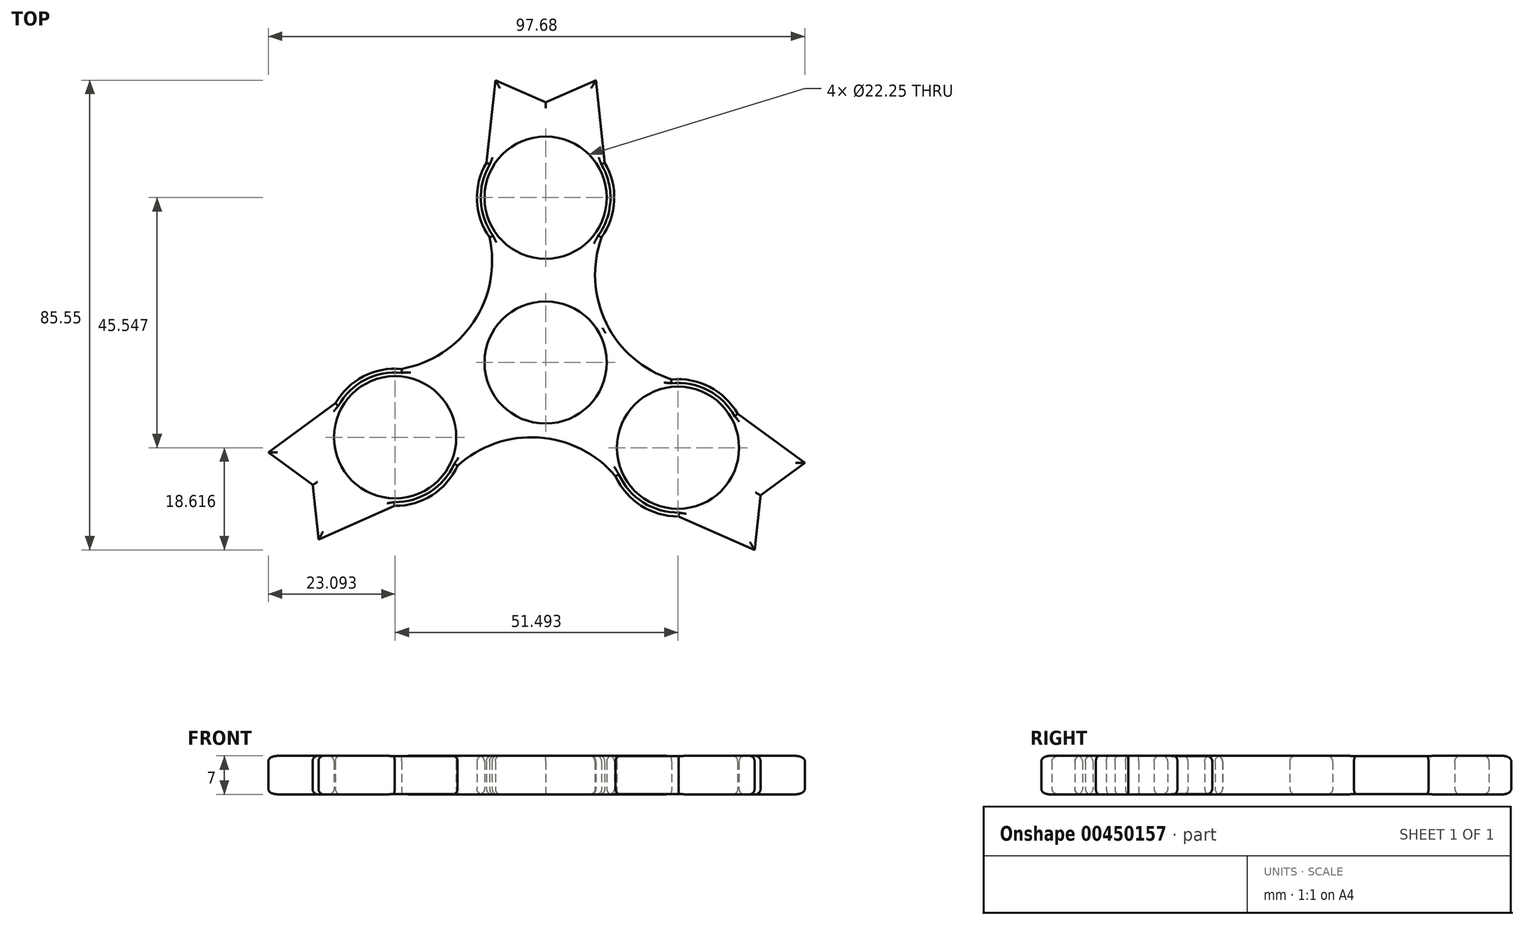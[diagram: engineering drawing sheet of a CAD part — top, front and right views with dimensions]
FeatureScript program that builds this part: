
annotation { "Feature Type Name" : "Feature", "Feature Type Description" : "" }
export const myFeature = defineFeature(function(context is Context, id is Id, definition is map)
    precondition{}
    {
        {
            var Q0;
            Q0=qCreatedBy(makeId("Top.planeOp"),FACE);
            var sketch = newSketch(context, id + "F0", { "sketchPlane" : qUnion([Q0])});
            skCircle(sketch, "E0", {"center": v(0, 0) * mm, "radius": 11.13 * mm});
            skLineSegment(sketch, "E1", {"start": v(32.45, -16.12) * mm, "end": v(32.45, -21.33) * mm, "construction": true});
            skLineSegment(sketch, "E2", {"start": v(-9.15, 36.82) * mm, "end": v(9.15, 36.82) * mm, "construction": true});
            skLineSegment(sketch, "E3", {"start": v(-10.78, 36.35) * mm, "end": v(-9.15, 51.4) * mm});
            skLineSegment(sketch, "E4", {"start": v(-9.15, 51.4) * mm, "end": v(0, 47.38) * mm});
            skLineSegment(sketch, "E5", {"start": v(0, 47.38) * mm, "end": v(9.15, 51.4) * mm});
            skLineSegment(sketch, "E6", {"start": v(9.15, 51.4) * mm, "end": v(10.78, 36.35) * mm});
            skCircle(sketch, "E7", {"center": v(0, 30.02) * mm, "radius": 11.13 * mm});
            skLineSegment(sketch, "E8", {"start": v(-11.33, 31.25) * mm, "end": v(11.33, 31.25) * mm, "construction": true});
            skArc(sketch, "E9", {"start": v(-10.78, 36.35) * mm, "mid": v(-12.49, 29.48) * mm, "end": v(-10.19, 22.78) * mm});
            skCircle(sketch, "E10.1.0", {"center": v(-27.4, -13.62) * mm, "radius": 11.13 * mm});
            skLineSegment(sketch, "E10.1.1", {"start": v(-50.5, -16.38) * mm, "end": v(-38.27, -7.45) * mm});
            skLineSegment(sketch, "E10.1.2", {"start": v(-42.43, -22.3) * mm, "end": v(-50.5, -16.38) * mm});
            skLineSegment(sketch, "E10.1.3", {"start": v(-41.34, -32.24) * mm, "end": v(-42.43, -22.3) * mm});
            skLineSegment(sketch, "E10.1.4", {"start": v(-27.49, -26.12) * mm, "end": v(-41.34, -32.24) * mm});
            skArc(sketch, "E10.1.5", {"start": v(-27.49, -26.12) * mm, "mid": v(-20.68, -24.16) * mm, "end": v(-16.03, -18.82) * mm});
            skCircle(sketch, "E10.2.0", {"center": v(24.1, -15.52) * mm, "radius": 11.13 * mm});
            skLineSegment(sketch, "E10.2.1", {"start": v(38.04, -34.14) * mm, "end": v(24.19, -28.02) * mm});
            skLineSegment(sketch, "E10.2.2", {"start": v(39.13, -24.2) * mm, "end": v(38.04, -34.14) * mm});
            skLineSegment(sketch, "E10.2.3", {"start": v(47.2, -18.29) * mm, "end": v(39.13, -24.2) * mm});
            skLineSegment(sketch, "E10.2.4", {"start": v(34.97, -9.35) * mm, "end": v(47.2, -18.29) * mm});
            skArc(sketch, "E10.2.5", {"start": v(34.97, -9.35) * mm, "mid": v(13.27, -9.27) * mm, "end": v(24.19, -28.02) * mm});
            skPoint(sketch, "E10.center", {"position": v(-1.1, 0.3) * mm});
            skArc(sketch, "E11", {"start": v(12.73, -20.73) * mm, "mid": v(-1.24, -13.65) * mm, "end": v(-16.03, -18.82) * mm});
            skLineSegment(sketch, "E12", {"start": v(-16.03, -18.82) * mm, "end": v(-27.49, -26.12) * mm, "construction": true});
            skLineSegment(sketch, "E13", {"start": v(12.73, -20.73) * mm, "end": v(24.19, -28.02) * mm, "construction": true});
            skArc(sketch, "E14", {"start": v(10.19, 22.78) * mm, "mid": v(11.05, 7.14) * mm, "end": v(22.92, -3.08) * mm});
            skArc(sketch, "E15", {"start": v(-26.22, -1.17) * mm, "mid": v(-13.1, 7.4) * mm, "end": v(-10.19, 22.78) * mm});
            skLineSegment(sketch, "E16", {"start": v(-26.22, -1.17) * mm, "end": v(-38.27, -7.45) * mm, "construction": true});
            skLineSegment(sketch, "E17", {"start": v(-10.3, 25.12) * mm, "end": v(-10.32, 25.88) * mm, "construction": true});
            skLineSegment(sketch, "E18", {"start": v(10.19, 22.78) * mm, "end": v(10.78, 36.35) * mm, "construction": true});
            skLineSegment(sketch, "E19.trimOffspring", {"start": v(-10.56, 31.25) * mm, "end": v(-10.78, 36.35) * mm, "construction": true});
            skArc(sketch, "E20.trimOffspring", {"start": v(10.19, 22.78) * mm, "mid": v(12.49, 29.48) * mm, "end": v(10.78, 36.35) * mm});
            skArc(sketch, "E21.trimOffspring", {"start": v(-26.22, -1.17) * mm, "mid": v(-33.17, -2.53) * mm, "end": v(-38.27, -7.45) * mm});
            skSolve(sketch);
        }
        {
            var Q0;
            Q0 = qSketchRegion(id + "F0", true);
            extrude(context, id + "F1", {"entities" : qUnion([Q0]), "depth" : 7 * mm, "offsetDistance" : 25 * mm});
        }
        {
            var Q0;
            Q0=makeQuery(id+"F1.opExtrude","CAP_FACE",FACE,{"disambiguationData":[OSD([sQuery(id+"F0.wireOp",EDGE,"E0"),sQuery(id+"F0.wireOp",EDGE,"E3"),sQuery(id+"F0.wireOp",EDGE,"E4"),sQuery(id+"F0.wireOp",EDGE,"E5"),sQuery(id+"F0.wireOp",EDGE,"E6"),sQuery(id+"F0.wireOp",EDGE,"E7"),sQuery(id+"F0.wireOp",EDGE,"E9"),sQuery(id+"F0.wireOp",EDGE,"E10.1.0"),sQuery(id+"F0.wireOp",EDGE,"E10.1.1"),sQuery(id+"F0.wireOp",EDGE,"E10.1.2"),sQuery(id+"F0.wireOp",EDGE,"E10.1.3"),sQuery(id+"F0.wireOp",EDGE,"E10.1.4"),sQuery(id+"F0.wireOp",EDGE,"E10.1.5"),sQuery(id+"F0.wireOp",EDGE,"E10.2.0"),sQuery(id+"F0.wireOp",EDGE,"E10.2.1"),sQuery(id+"F0.wireOp",EDGE,"E10.2.2"),sQuery(id+"F0.wireOp",EDGE,"E10.2.3"),sQuery(id+"F0.wireOp",EDGE,"E10.2.4"),sQuery(id+"F0.wireOp",EDGE,"E10.2.5"),sQuery(id+"F0.wireOp",EDGE,"E11"),sQuery(id+"F0.wireOp",EDGE,"E14"),sQuery(id+"F0.wireOp",EDGE,"E15"),sQuery(id+"F0.wireOp",EDGE,"E20.trimOffspring"),sQuery(id+"F0.wireOp",EDGE,"E21.trimOffspring")])],"isStart":false});
            fillet(context, id + "F2", {"entities" : qUnion([Q0]), "radius" : 1 * mm, "tangentPropagation" : true, "allowEdgeOverflow" : false});
        }
        {
            var Q0;
            Q0=makeQuery(id+"F1.opExtrude","CAP_FACE",FACE,{"disambiguationData":[OSD([sQuery(id+"F0.wireOp",EDGE,"E0"),sQuery(id+"F0.wireOp",EDGE,"E3"),sQuery(id+"F0.wireOp",EDGE,"E4"),sQuery(id+"F0.wireOp",EDGE,"E5"),sQuery(id+"F0.wireOp",EDGE,"E6"),sQuery(id+"F0.wireOp",EDGE,"E7"),sQuery(id+"F0.wireOp",EDGE,"E9"),sQuery(id+"F0.wireOp",EDGE,"E10.1.0"),sQuery(id+"F0.wireOp",EDGE,"E10.1.1"),sQuery(id+"F0.wireOp",EDGE,"E10.1.2"),sQuery(id+"F0.wireOp",EDGE,"E10.1.3"),sQuery(id+"F0.wireOp",EDGE,"E10.1.4"),sQuery(id+"F0.wireOp",EDGE,"E10.1.5"),sQuery(id+"F0.wireOp",EDGE,"E10.2.0"),sQuery(id+"F0.wireOp",EDGE,"E10.2.1"),sQuery(id+"F0.wireOp",EDGE,"E10.2.2"),sQuery(id+"F0.wireOp",EDGE,"E10.2.3"),sQuery(id+"F0.wireOp",EDGE,"E10.2.4"),sQuery(id+"F0.wireOp",EDGE,"E10.2.5"),sQuery(id+"F0.wireOp",EDGE,"E11"),sQuery(id+"F0.wireOp",EDGE,"E14"),sQuery(id+"F0.wireOp",EDGE,"E15"),sQuery(id+"F0.wireOp",EDGE,"E20.trimOffspring"),sQuery(id+"F0.wireOp",EDGE,"E21.trimOffspring")])],"isStart":true});
            fillet(context, id + "F3", {"entities" : qUnion([Q0]), "radius" : 1 * mm, "tangentPropagation" : true, "allowEdgeOverflow" : false});
        }
    });
